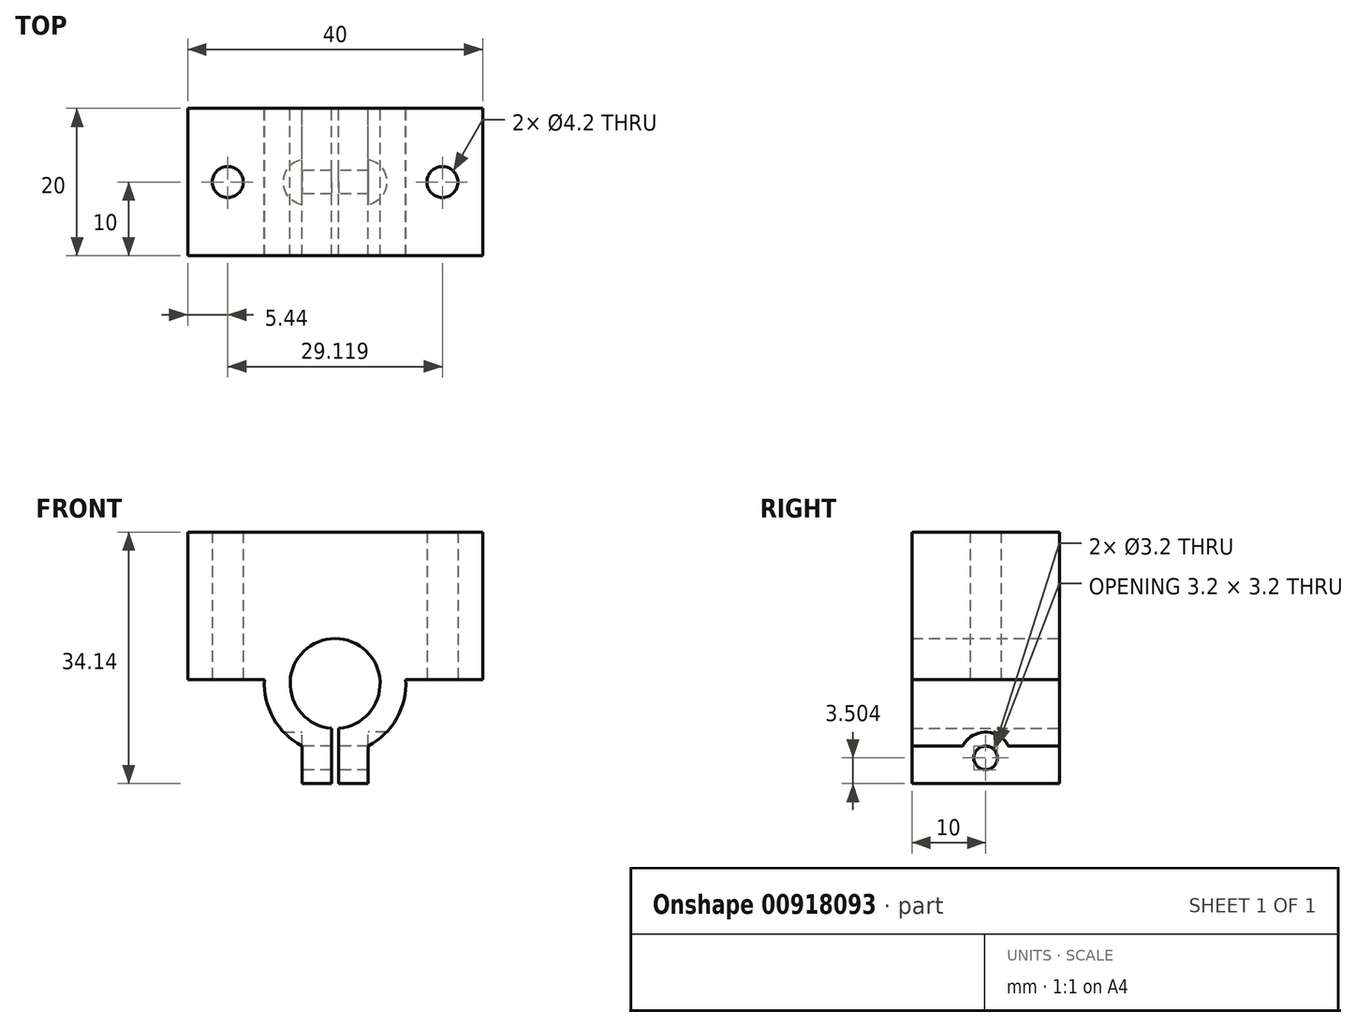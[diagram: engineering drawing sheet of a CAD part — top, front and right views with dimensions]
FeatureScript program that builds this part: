
annotation { "Feature Type Name" : "Feature", "Feature Type Description" : "" }
export const myFeature = defineFeature(function(context is Context, id is Id, definition is map)
    precondition{}
    {
        {
            var Q0;
            Q0=qCreatedBy(makeId("Front.planeOp"),FACE);
            var sketch = newSketch(context, id + "F0", { "sketchPlane" : qUnion([Q0])});
            skArc(sketch, "E0", {"start": v(0.5, -6.08) * mm, "mid": v(0, 6.1) * mm, "end": v(-0.5, -6.08) * mm});
            skLineSegment(sketch, "E1", {"start": v(-6.1, 0) * mm, "end": v(-9.6, 0) * mm});
            skLineSegment(sketch, "E2", {"start": v(6.1, 0) * mm, "end": v(9.6, 0) * mm});
            skArc(sketch, "E3", {"start": v(4.5, -8.48) * mm, "mid": v(0, 9.6) * mm, "end": v(-4.5, -8.48) * mm});
            skLineSegment(sketch, "E4", {"start": v(0, 0) * mm, "end": v(0, 3) * mm});
            skLineSegment(sketch, "E5", {"start": v(-5.31, 3) * mm, "end": v(-20, 3) * mm});
            skLineSegment(sketch, "E6", {"start": v(5.31, 3) * mm, "end": v(20, 3) * mm});
            skLineSegment(sketch, "E7", {"start": v(-20, 3) * mm, "end": v(-20, 13) * mm});
            skLineSegment(sketch, "E8", {"start": v(-20, 13) * mm, "end": v(20, 13) * mm});
            skLineSegment(sketch, "E9", {"start": v(20, 13) * mm, "end": v(20, 3) * mm});
            skLineSegment(sketch, "E10", {"start": v(0, 0) * mm, "end": v(-0.5, 0) * mm});
            skLineSegment(sketch, "E11", {"start": v(0, 0) * mm, "end": v(0.5, 0) * mm});
            skLineSegment(sketch, "E12", {"start": v(4.5, -13.59) * mm, "end": v(4.5, -8.48) * mm});
            skLineSegment(sketch, "E13", {"start": v(-4.5, -13.59) * mm, "end": v(-4.5, -8.48) * mm});
            skLineSegment(sketch, "E14", {"start": v(-0.5, -6.08) * mm, "end": v(-0.5, -13.59) * mm});
            skLineSegment(sketch, "E15", {"start": v(0.5, -6.08) * mm, "end": v(0.5, -13.59) * mm});
            skLineSegment(sketch, "E16", {"start": v(0.5, -13.59) * mm, "end": v(4.5, -13.59) * mm});
            skLineSegment(sketch, "E17", {"start": v(-0.5, -13.59) * mm, "end": v(-4.5, -13.59) * mm});
            skSolve(sketch);
        }
        {
            var Q0;
            Q0=qSketchRegion(id+"F0",true);
            extrude(context, id + "F1", {"entities" : qUnion([Q0]), "depth" : 20 * mm});
        }
        {
            var Q0;
            Q0=makeQuery(id+"F1.opExtrude","SWEPT_FACE",FACE,{"disambiguationData":[OSD([sQuery(id+"F0.wireOp",EDGE,"E5")])]});
            var sketch = newSketch(context, id + "F2", { "sketchPlane" : qUnion([Q0])});
            skLineSegment(sketch, "E18", {"start": v(-14.56, 20) * mm, "end": v(-14.56, 0) * mm});
            skCircle(sketch, "E19", {"center": v(-14.56, 10) * mm, "radius": 2.1 * mm});
            skSolve(sketch);
        }
        {
            var Q0;
            Q0=qSketchRegion(id+"F2",true);
            extrude(context, id + "F3", {"entities" : qUnion([Q0]), "operationType" : NewBodyOperationType.REMOVE, "oppositeDirection" : true, "depth" : 25 * mm});
        }
        {
            var Q0;
            Q0=makeQuery(id+"F1.opExtrude","SWEPT_FACE",FACE,{"disambiguationData":[OSD([sQuery(id+"F0.wireOp",EDGE,"E6")])]});
            var sketch = newSketch(context, id + "F4", { "sketchPlane" : qUnion([Q0])});
            skLineSegment(sketch, "E20", {"start": v(14.56, 20) * mm, "end": v(14.56, 0) * mm});
            skCircle(sketch, "E21", {"center": v(14.56, 10) * mm, "radius": 2.1 * mm});
            skSolve(sketch);
        }
        {
            var Q0;
            Q0=qSketchRegion(id+"F4",true);
            extrude(context, id + "F5", {"entities" : qUnion([Q0]), "operationType" : NewBodyOperationType.REMOVE, "oppositeDirection" : true, "depth" : 25 * mm});
        }
        {
            var Q0;
            Q0=makeQuery(id+"F1.opExtrude","SWEPT_FACE",FACE,{"disambiguationData":[OSD([sQuery(id+"F0.wireOp",EDGE,"E13")])]});
            var sketch = newSketch(context, id + "F6", { "sketchPlane" : qUnion([Q0])});
            skLineSegment(sketch, "E22", {"start": v(10, -13.59) * mm, "end": v(10, -6.59) * mm});
            skCircle(sketch, "E23", {"center": v(10, -10.09) * mm, "radius": 1.6 * mm});
            skSolve(sketch);
        }
        {
            var Q0;
            Q0=qSketchRegion(id+"F6",true);
            extrude(context, id + "F7", {"entities" : qUnion([Q0]), "operationType" : NewBodyOperationType.REMOVE, "oppositeDirection" : true, "depth" : 25 * mm});
        }
        {
            var Q0;
            Q0=makeQuery(id+"F1.opExtrude","SWEPT_FACE",FACE,{"disambiguationData":[OSD([sQuery(id+"F0.wireOp",EDGE,"E13")])]});
            var sketch = newSketch(context, id + "F8", { "sketchPlane" : qUnion([Q0])});
            skCircle(sketch, "E24", {"center": v(10, -10.09) * mm, "radius": 3.5 * mm});
            skSolve(sketch);
        }
        {
            var Q0;
            Q0=qSketchRegion(id+"F8",true);
            extrude(context, id + "F9", {"entities" : qUnion([Q0]), "operationType" : NewBodyOperationType.REMOVE, "depth" : 25 * mm});
        }
        {
            var Q0;
            Q0=makeQuery(id+"F1.opExtrude","SWEPT_FACE",FACE,{"disambiguationData":[OSD([sQuery(id+"F0.wireOp",EDGE,"E12")])]});
            var sketch = newSketch(context, id + "F10", { "sketchPlane" : qUnion([Q0])});
            skCircle(sketch, "E25", {"center": v(-10, -10.09) * mm, "radius": 3.5 * mm});
            skSolve(sketch);
        }
        {
            var Q0;
            Q0=qSketchRegion(id+"F10",true);
            extrude(context, id + "F11", {"entities" : qUnion([Q0]), "operationType" : NewBodyOperationType.REMOVE, "depth" : 25 * mm});
        }
        {
            var Q0;
            Q0=qSketchRegion(id+"F8",true);
            extrude(context, id + "F12", {"entities" : qUnion([Q0]), "operationType" : NewBodyOperationType.REMOVE, "depth" : 25 * mm});
        }
        {
            var Q0;
            Q0=makeQuery(id+"F1.opExtrude","SWEPT_FACE",FACE,{"disambiguationData":[OSD([sQuery(id+"F0.wireOp",EDGE,"E8")])]});
            var sketch = newSketch(context, id + "F13", { "sketchPlane" : qUnion([Q0])});
            skLineSegment(sketch, "E26.bottom", {"start": v(20, -20) * mm, "end": v(-20, -20) * mm});
            skLineSegment(sketch, "E26.top", {"start": v(20, 0) * mm, "end": v(-20, 0) * mm});
            skLineSegment(sketch, "E26.left", {"start": v(20, -20) * mm, "end": v(20, 0) * mm});
            skLineSegment(sketch, "E26.right", {"start": v(-20, -20) * mm, "end": v(-20, 0) * mm});
            skCircle(sketch, "E27", {"center": v(14.56, -10) * mm, "radius": 2.1 * mm});
            skCircle(sketch, "E28", {"center": v(-14.56, -10) * mm, "radius": 2.1 * mm});
            skSolve(sketch);
        }
        {
            var Q0;
            Q0=qSketchRegion(id+"F13",true);
            extrude(context, id + "F14", {"entities" : qUnion([Q0]), "operationType" : NewBodyOperationType.ADD, "depth" : 7.55 * mm});
        }
        {
            var Q0;
            Q0=makeQuery(id+"F1.opExtrude","SWEPT_FACE",FACE,{"disambiguationData":[OSD([sQuery(id+"F0.wireOp",EDGE,"E5")])]});
            var sketch = newSketch(context, id + "F15", { "sketchPlane" : qUnion([Q0])});
            skLineSegment(sketch, "E29.bottom", {"start": v(-20, 20) * mm, "end": v(-9.12, 20) * mm});
            skLineSegment(sketch, "E29.top", {"start": v(-20, 0) * mm, "end": v(-9.12, 0) * mm});
            skLineSegment(sketch, "E29.left", {"start": v(-20, 20) * mm, "end": v(-20, 0) * mm});
            skLineSegment(sketch, "E29.right", {"start": v(-9.12, 20) * mm, "end": v(-9.12, 0) * mm});
            skCircle(sketch, "E30", {"center": v(-14.56, 10) * mm, "radius": 2.1 * mm});
            skSolve(sketch);
        }
        {
            var Q0;
            Q0=makeQuery(id+"F1.opExtrude","SWEPT_FACE",FACE,{"disambiguationData":[OSD([sQuery(id+"F0.wireOp",EDGE,"E6")])]});
            var sketch = newSketch(context, id + "F16", { "sketchPlane" : qUnion([Q0])});
            skLineSegment(sketch, "E31.bottom", {"start": v(20, 20) * mm, "end": v(9.12, 20) * mm});
            skLineSegment(sketch, "E31.top", {"start": v(20, 0) * mm, "end": v(9.12, 0) * mm});
            skLineSegment(sketch, "E31.left", {"start": v(20, 20) * mm, "end": v(20, 0) * mm});
            skLineSegment(sketch, "E31.right", {"start": v(9.12, 20) * mm, "end": v(9.12, 0) * mm});
            skCircle(sketch, "E32", {"center": v(14.56, 10) * mm, "radius": 2.1 * mm});
            skSolve(sketch);
        }
        {
            var Q0;
            Q0=qSketchRegion(id+"F16",true);
            var Q1;
            Q1=makeQuery(id+"F15.imprint","IMPRINT",FACE,{"disambiguationData":[TD([[makeQuery(id+"F15.imprint","IMPRINT",EDGE,{"derivedFrom":sQuery(id+"F15.wireOp",EDGE,"E29.bottom")}),1.0]])]});
            extrude(context, id + "F17", {"entities" : qUnion([Q0, Q1]), "operationType" : NewBodyOperationType.ADD, "depth" : 2.45 * mm});
        }
    });
